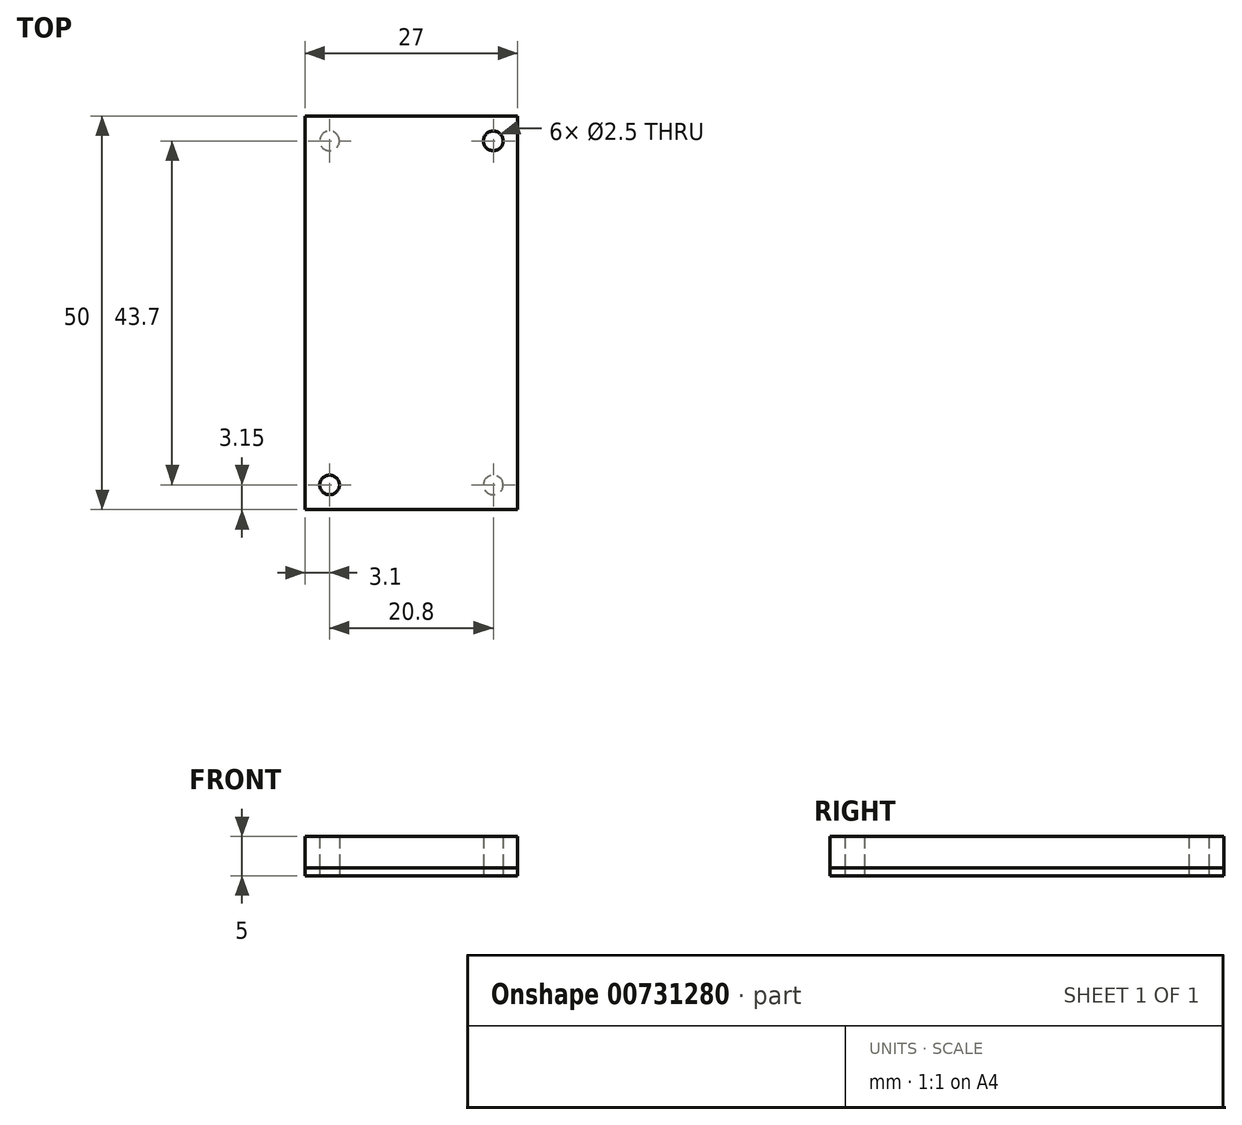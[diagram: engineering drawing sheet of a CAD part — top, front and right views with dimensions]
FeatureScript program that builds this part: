
annotation { "Feature Type Name" : "Feature", "Feature Type Description" : "" }
export const myFeature = defineFeature(function(context is Context, id is Id, definition is map)
    precondition{}
    {
        {
            var Q0;
            Q0=qCreatedBy(makeId("Top.planeOp"),FACE);
            var sketch = newSketch(context, id + "F0", { "sketchPlane" : qUnion([Q0])});
            skLineSegment(sketch, "E0.bottom", {"start": v(-13.5, 25) * mm, "end": v(13.5, 25) * mm});
            skLineSegment(sketch, "E0.top", {"start": v(-13.5, -25) * mm, "end": v(13.5, -25) * mm});
            skLineSegment(sketch, "E0.left", {"start": v(-13.5, 25) * mm, "end": v(-13.5, -25) * mm});
            skLineSegment(sketch, "E0.right", {"start": v(13.5, 25) * mm, "end": v(13.5, -25) * mm});
            skPoint(sketch, "E0.middle", {"position": v(0, 0) * mm});
            skCircle(sketch, "E1", {"center": v(-10.4, 21.85) * mm, "radius": 1.25 * mm});
            skLineSegment(sketch, "E2", {"start": v(0, 0) * mm, "end": v(0, 7.05) * mm});
            skLineSegment(sketch, "E3", {"start": v(0, 7.05) * mm, "end": v(0, 0) * mm});
            skLineSegment(sketch, "E4", {"start": v(0, 0) * mm, "end": v(2.77, 0) * mm});
            skCircle(sketch, "E5.MirrorC", {"center": v(10.4, 21.85) * mm, "radius": 1.25 * mm});
            skCircle(sketch, "E6.MirrorC", {"center": v(10.4, -21.85) * mm, "radius": 1.25 * mm});
            skCircle(sketch, "E7.MirrorC", {"center": v(-10.4, -21.85) * mm, "radius": 1.25 * mm});
            skSolve(sketch);
        }
        {
            var Q0;
            Q0=makeQuery(id+"F0.imprint","IMPRINT",FACE,{"disambiguationData":[TD([[makeQuery(id+"F0.imprint","IMPRINT",EDGE,{"derivedFrom":sQuery(id+"F0.wireOp",EDGE,"E1")}),1.0]])]});
            var Q1;
            Q1=makeQuery(id+"F0.imprint","IMPRINT",FACE,{"disambiguationData":[TD([[makeQuery(id+"F0.imprint","IMPRINT",EDGE,{"derivedFrom":sQuery(id+"F0.wireOp",EDGE,"E7.MirrorC")}),-1.0]])]});
            var Q2;
            Q2=makeQuery(id+"F0.imprint","IMPRINT",FACE,{"disambiguationData":[TD([[makeQuery(id+"F0.imprint","IMPRINT",EDGE,{"derivedFrom":sQuery(id+"F0.wireOp",EDGE,"E6.MirrorC")}),1.0]])]});
            var Q3;
            Q3=makeQuery(id+"F0.imprint","IMPRINT",FACE,{"disambiguationData":[TD([[makeQuery(id+"F0.imprint","IMPRINT",EDGE,{"derivedFrom":sQuery(id+"F0.wireOp",EDGE,"E5.MirrorC")}),-1.0]])]});
            extrude(context, id + "F1", {"entities" : qUnion([Q0, Q1, Q2, Q3]), "depth" : 5 * mm, "offsetDistance" : 25 * mm});
        }
        {
            var Q0;
            Q0=makeQuery(id+"F0.imprint","IMPRINT",FACE,{"disambiguationData":[TD([[makeQuery(id+"F0.imprint","IMPRINT",EDGE,{"derivedFrom":sQuery(id+"F0.wireOp",EDGE,"E0.bottom")}),-1.0]])]});
            extrude(context, id + "F2", {"entities" : qUnion([Q0]), "depth" : 1 * mm, "offsetDistance" : 25 * mm});
        }
    });
